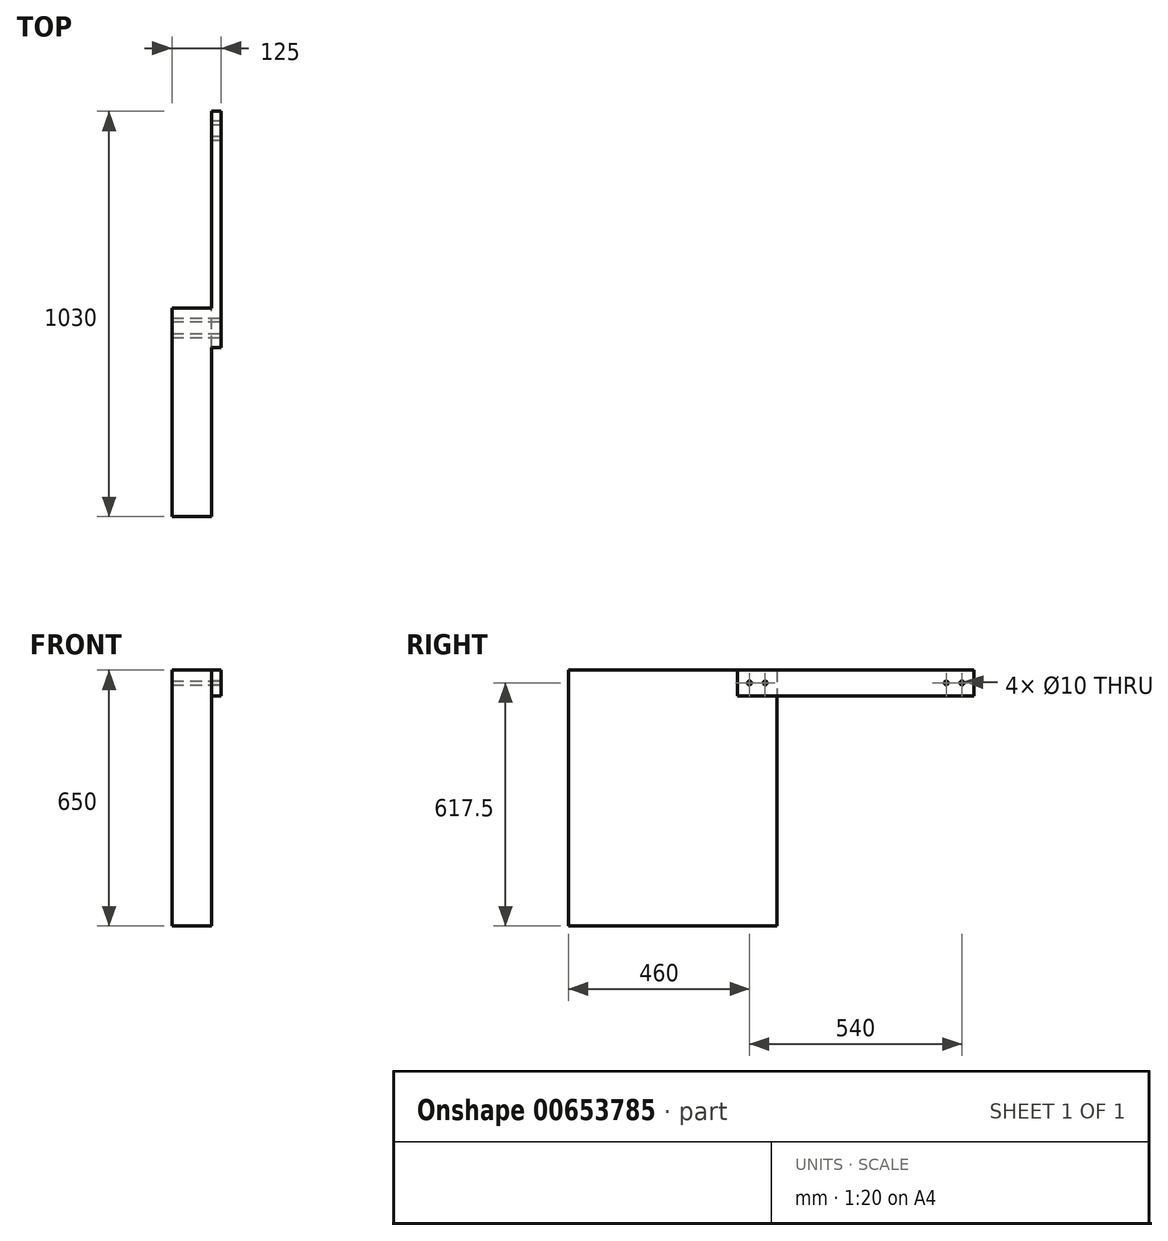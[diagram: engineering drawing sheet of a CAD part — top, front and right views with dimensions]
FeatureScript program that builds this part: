
annotation { "Feature Type Name" : "Feature", "Feature Type Description" : "" }
export const myFeature = defineFeature(function(context is Context, id is Id, definition is map)
    precondition{}
    {
        {
            var Q0;
            Q0=qCreatedBy(makeId("Top.planeOp"),FACE);
            var sketch = newSketch(context, id + "F0", { "sketchPlane" : qUnion([Q0])});
            skLineSegment(sketch, "E0.bottom", {"start": v(-100, -100) * mm, "end": v(0, -100) * mm});
            skLineSegment(sketch, "E0.top", {"start": v(-100, 0) * mm, "end": v(0, 0) * mm});
            skLineSegment(sketch, "E0.left", {"start": v(-100, -100) * mm, "end": v(-100, 0) * mm});
            skLineSegment(sketch, "E0.right", {"start": v(0, -100) * mm, "end": v(0, 0) * mm});
            skSolve(sketch);
        }
        {
            var Q0;
            Q0=qSketchRegion(id+"F0",true);
            extrude(context, id + "F1", {"entities" : qUnion([Q0]), "depth" : 650 * mm, "offsetDistance" : 25 * mm});
        }
        {
            var Q0;
            Q0=makeQuery(id+"F1.opExtrude","SWEPT_FACE",FACE,{"disambiguationData":[OSD([sQuery(id+"F0.wireOp",EDGE,"E0.right")])]});
            var sketch = newSketch(context, id + "F2", { "sketchPlane" : qUnion([Q0])});
            skCircle(sketch, "E1", {"center": v(-70, 617.5) * mm, "radius": 5 * mm});
            skCircle(sketch, "E2", {"center": v(-30, 617.5) * mm, "radius": 5 * mm});
            skSolve(sketch);
        }
        {
            var Q0;
            Q0=qSketchRegion(id+"F2",true);
            extrude(context, id + "F3", {"entities" : qUnion([Q0]), "operationType" : NewBodyOperationType.REMOVE, "endBound" : BoundingType.THROUGH_ALL, "oppositeDirection" : true, "depth" : 25 * mm, "offsetDistance" : 25 * mm});
        }
        {
            var Q0;
            Q0=qCreatedBy(makeId("Right.planeOp"),FACE);
            var sketch = newSketch(context, id + "F4", { "sketchPlane" : qUnion([Q0])});
            skLineSegment(sketch, "E3.bottom", {"start": v(-100, 650) * mm, "end": v(500, 650) * mm});
            skLineSegment(sketch, "E3.top", {"start": v(-100, 585) * mm, "end": v(500, 585) * mm});
            skLineSegment(sketch, "E3.left", {"start": v(-100, 650) * mm, "end": v(-100, 585) * mm});
            skLineSegment(sketch, "E3.right", {"start": v(500, 650) * mm, "end": v(500, 585) * mm});
            skCircle(sketch, "E4", {"center": v(-70, 617.5) * mm, "radius": 5 * mm});
            skCircle(sketch, "E5", {"center": v(-30, 617.5) * mm, "radius": 5 * mm});
            skLineSegment(sketch, "E6", {"start": v(200, 650) * mm, "end": v(200, 585) * mm, "construction": true});
            skCircle(sketch, "E7.MirrorC", {"center": v(470, 617.5) * mm, "radius": 5 * mm});
            skCircle(sketch, "E8.MirrorC", {"center": v(430, 617.5) * mm, "radius": 5 * mm});
            skSolve(sketch);
        }
        {
            var Q0;
            Q0=makeQuery(id+"F4.imprint","IMPRINT",FACE,{"disambiguationData":[TD([[makeQuery(id+"F4.imprint","IMPRINT",EDGE,{"derivedFrom":sQuery(id+"F4.wireOp",EDGE,"E3.bottom")}),-1.0]])]});
            extrude(context, id + "F5", {"entities" : qUnion([Q0]), "depth" : 25 * mm, "offsetDistance" : 25 * mm});
        }
        {
            var Q0;
            Q0=makeQuery(id+"F1.opExtrude","SWEPT_FACE",FACE,{"disambiguationData":[OSD([sQuery(id+"F0.wireOp",EDGE,"E0.bottom")])]});
            extrude(context, id + "F6", {"entities" : qUnion([Q0]), "operationType" : NewBodyOperationType.ADD, "depth" : 430 * mm, "offsetDistance" : 25 * mm});
        }
    });
